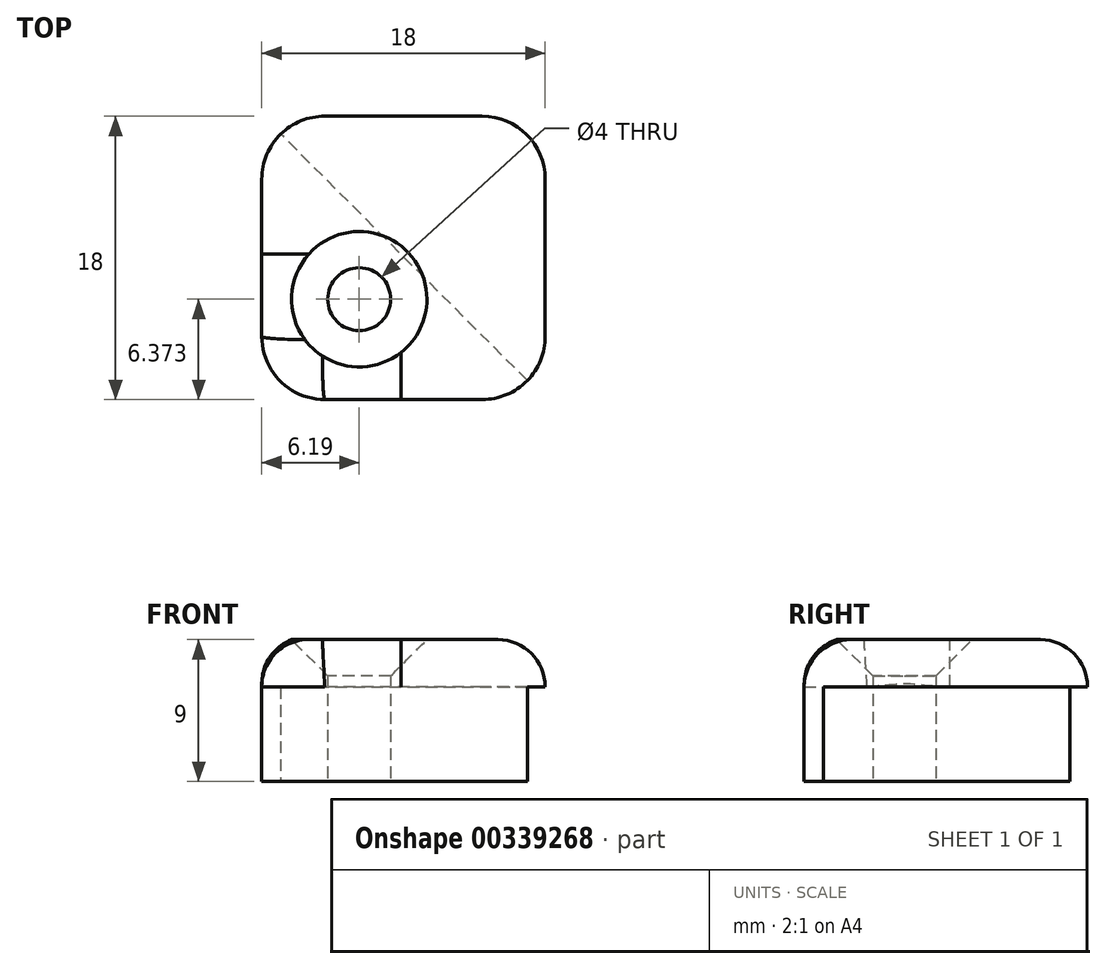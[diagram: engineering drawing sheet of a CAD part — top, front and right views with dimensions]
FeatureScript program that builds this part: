
annotation { "Feature Type Name" : "Feature", "Feature Type Description" : "" }
export const myFeature = defineFeature(function(context is Context, id is Id, definition is map)
    precondition{}
    {
        {
            var Q0;
            Q0=qCreatedBy(makeId("Top.planeOp"),FACE);
            var sketch = newSketch(context, id + "F0", { "sketchPlane" : qUnion([Q0])});
            skLineSegment(sketch, "E0.bottom", {"start": v(5, -9) * mm, "end": v(-5, -9) * mm});
            skLineSegment(sketch, "E0.top", {"start": v(5, 9) * mm, "end": v(-5, 9) * mm});
            skLineSegment(sketch, "E0.left", {"start": v(9, -5) * mm, "end": v(9, 5) * mm});
            skLineSegment(sketch, "E0.right", {"start": v(-9, -5) * mm, "end": v(-9, 5) * mm});
            skPoint(sketch, "E0.middle", {"position": v(0, 0) * mm});
            skPoint(sketch, "E1.visualSharp", {"position": v(-9, 9) * mm});
            skArc(sketch, "E1.filletArc", {"start": v(-5, 9) * mm, "mid": v(-7.83, 7.83) * mm, "end": v(-9, 5) * mm});
            skPoint(sketch, "E2.visualSharp", {"position": v(9, 9) * mm});
            skArc(sketch, "E2.filletArc", {"start": v(9, 5) * mm, "mid": v(7.83, 7.83) * mm, "end": v(5, 9) * mm});
            skPoint(sketch, "E3.visualSharp", {"position": v(9, -9) * mm});
            skArc(sketch, "E3.filletArc", {"start": v(5, -9) * mm, "mid": v(7.83, -7.83) * mm, "end": v(9, -5) * mm});
            skPoint(sketch, "E4.visualSharp", {"position": v(-9, -9) * mm});
            skArc(sketch, "E4.filletArc", {"start": v(-9, -5) * mm, "mid": v(-7.83, -7.83) * mm, "end": v(-5, -9) * mm});
            skCircle(sketch, "E5", {"center": v(-2.81, -2.63) * mm, "radius": 2 * mm});
            skSolve(sketch);
        }
        {
            var Q0;
            Q0 = qSketchRegion(id + "F0", true);
            extrude(context, id + "F1", {"entities" : qUnion([Q0]), "depth" : 9 * mm});
        }
        {
            var Q0;
            Q0=makeQuery(id+"F1.opExtrude","CAP_EDGE",EDGE,{"disambiguationData":[OSD([sQuery(id+"F0.wireOp",EDGE,"E5")])],"isStart":false});
            chamfer(context, id + "F2", {"entities" : qUnion([Q0]), "width" : 2.3 * mm, "tangentPropagation" : true});
        }
        {
            var Q0;
            Q0=makeQuery(id+"F1.opExtrude","CAP_EDGE",EDGE,{"disambiguationData":[OSD([sQuery(id+"F0.wireOp",EDGE,"E0.top")])],"isStart":false});
            var Q1;
            Q1=makeQuery(id+"F1.opExtrude","CAP_EDGE",EDGE,{"disambiguationData":[OSD([sQuery(id+"F0.wireOp",EDGE,"E1.filletArc")])],"isStart":false});
            var Q2;
            Q2=makeQuery(id+"F1.opExtrude","CAP_EDGE",EDGE,{"disambiguationData":[OSD([sQuery(id+"F0.wireOp",EDGE,"E0.right")])],"isStart":false});
            var Q3;
            Q3=makeQuery(id+"F1.opExtrude","CAP_EDGE",EDGE,{"disambiguationData":[OSD([sQuery(id+"F0.wireOp",EDGE,"E4.filletArc")])],"isStart":false});
            var Q4;
            Q4=makeQuery(id+"F1.opExtrude","CAP_EDGE",EDGE,{"disambiguationData":[OSD([sQuery(id+"F0.wireOp",EDGE,"E3.filletArc")])],"isStart":false});
            fillet(context, id + "F3", {"entities" : qUnion([Q0, Q1, Q2, Q3, Q4]), "radius" : 3 * mm, "tangentPropagation" : true, "allowEdgeOverflow" : false});
        }
        {
            var Q0;
            Q0=qCreatedBy(makeId("Top.planeOp"),FACE);
            cPlane(context, id + "F4", {"entities" : qUnion([Q0]), "cplaneType" : CPlaneType.OFFSET, "offset" : 10 * mm, "oppositeDirection" : true, "width" : 150 * mm, "height" : 150 * mm});
        }
        {
            var Q0;
            Q0=qCreatedBy(id+"F4.planeOp",FACE);
            var sketch = newSketch(context, id + "F5", { "sketchPlane" : qUnion([Q0])});
            skLineSegment(sketch, "E6", {"start": v(-8.9, 8.97) * mm, "end": v(12.65, -12.58) * mm});
            skLineSegment(sketch, "E7", {"start": v(12.65, -12.58) * mm, "end": v(12.65, 14.1) * mm});
            skLineSegment(sketch, "E8", {"start": v(12.65, 14.1) * mm, "end": v(-8.9, 8.97) * mm});
            skSolve(sketch);
        }
        {
            var Q0;
            Q0=makeQuery(id+"F5.imprint","IMPRINT",FACE,{"disambiguationData":[TD([[makeQuery(id+"F5.imprint","IMPRINT",EDGE,{"derivedFrom":sQuery(id+"F5.wireOp",EDGE,"E6")}),1.0]])]});
            extrude(context, id + "F6", {"entities" : qUnion([Q0]), "depth" : 16 * mm});
        }
        {
            var Q0;
            Q0=makeQuery(id+"F6.opExtrude","SWEPT_BODY",BODY,{"disambiguationData":[OSD([sQuery(id+"F5.wireOp",EDGE,"E6"),sQuery(id+"F5.wireOp",EDGE,"E7"),sQuery(id+"F5.wireOp",EDGE,"E8")])]});
            var Q1;
            Q1=makeQuery(id+"F1.opExtrude","SWEPT_BODY",BODY,{"disambiguationData":[OSD([sQuery(id+"F0.wireOp",EDGE,"E0.bottom"),sQuery(id+"F0.wireOp",EDGE,"E0.top"),sQuery(id+"F0.wireOp",EDGE,"E0.left"),sQuery(id+"F0.wireOp",EDGE,"E0.right"),sQuery(id+"F0.wireOp",EDGE,"E1.filletArc"),sQuery(id+"F0.wireOp",EDGE,"E2.filletArc"),sQuery(id+"F0.wireOp",EDGE,"E3.filletArc"),sQuery(id+"F0.wireOp",EDGE,"E4.filletArc"),sQuery(id+"F0.wireOp",EDGE,"E5")])]});
            booleanBodies(context, id + "F7", {"operationType" : BooleanOperationType.SUBTRACTION, "tools" : qUnion([Q0]), "targets" : qUnion([Q1])});
        }
    });
